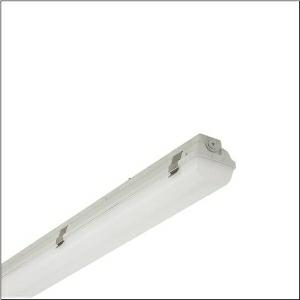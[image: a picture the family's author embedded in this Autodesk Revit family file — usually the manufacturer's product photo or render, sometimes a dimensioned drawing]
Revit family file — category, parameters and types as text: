
# Revit family: monsun_r__21_eco_51fj20ml45a_05e8
name_source: partatom
category: Lighting Fixtures
units: mm (PartAtom-declared; Revit-internal decimal feet)

## family parameters
Cut with Voids When Loaded = No
Host = Face
Light Source = No
Part Type = Normal
Room Calculation Point = No
Round Connector Dimension = Use Diameter
Shared = No

## types (1)
- --- (1 x LED, 4900 lm, 36 W, 4000K)
    Apparent Load = 36 VA
    CIE Flux Codes = 40 69 88 88 100
    Color Rendering = 80
    Color Temperature = 4000K
    Default Elevation = 1800 mm
    Description = Monsun® 21 Eco, damp-proof luminaire, primary optical cover: diffuser, of PC, UV-stabilised, frosted, light emission: direct distribution, primary light characteristic: symmetric, installation type: suspended mounting, surface-mounted, LED, rated luminous flux: 4.900lm, luminous efficacy: 132lm/W, light colour: 840, colour temperature: 4000K, control gear: ECG Multilumen, with terminal, 3-pole, max. 2.5mm², mains connection: 220..240V, AC, 50/60Hz, rated input power: 36W, housing, of glass-fibre reinforced polyester, light grey (RAL 7035), length: 1.277mm, width: 90mm, height: 95mm, clip for enclosure, of spring steel V2A, protection rating (complete): IP66, insulation class (complete): insulation class I (protective earthing), certification: CE, UKCA, protection symbol: D, impact resistance: IK08, permissible operating ambient temperature: -20..+35°C, corresponds to IFS (International Featured Standards) requirements for safety and quality in the food industry, packaging unit: 1 piece
    Height = 103 mm
    Lamp = 1 x LED
    Lamp Light Flux = 4900 lm
    Lamp Power = 36 W
    Lamp count = 1
    Length = 1277 mm
    Luminous efficacy = 136 lm/W
    Manufacturer = Siteco
    ModVariant = No
    Model = 51FJ20ML45A
    Mounting Place = Ceiling
    Mounting Type = Surface mounted
    Number of Poles = 1
    OnlyDefault = Yes
    Power Factor = 1
    Product Name = Monsun® 21 Eco
    Product group = damp-proof luminaire | ceiling mounted
    ProductGroupID = 300
    Protection Class = Protection class I
    Protection Degree = IP 66
    RLX_Detail_Level = 1
    RlxData = <blob elided: 33849 chars, md5=a9631da0>
    Socket = socket
    Standby Power = 0 W
    System Light Flux = 4900 lm
    System Power = 36 W
    Type Comments = factory setting: luminous flux: 100 % | (ON | ON) | 350 mA
    Type Image = l_1007218.jpg
    URL = http://relux.com
    VarID = @adj_055453
    Voltage = 0 V
    Weight = 0.00 kg
    Width = 90 mm

## geometry (parser evidence)
native form markers: Blend x4, Sweep x10
no freeform markers — native parametric forms only
